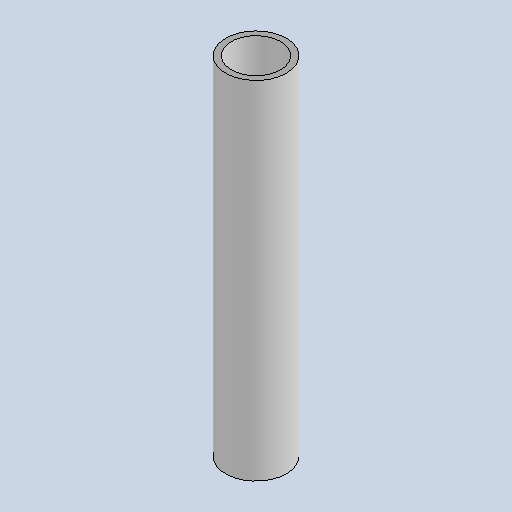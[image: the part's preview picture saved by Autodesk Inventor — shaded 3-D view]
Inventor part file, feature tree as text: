
AUTODESK INVENTOR PART (.ipt)
format: ipt  version: 2025.1 (Build 291241020, 241B)  size: 117,248 bytes
history: native  units: mm
features: extrude x1, sketch x1
ambient origin geometry x8: Origin, YZ Plane, XZ Plane, XY Plane, X Axis, Y Axis, Z Axis, Center Point
bodies: Body1 (feature_tree)
feature tree (2):
  extrude  "Extrusion5"  Depth=120.0mm
  sketch  "Sketch11"  dims[d187=21.0mm d188=2.0mm d189=120.0mm d190=0.0mm]
